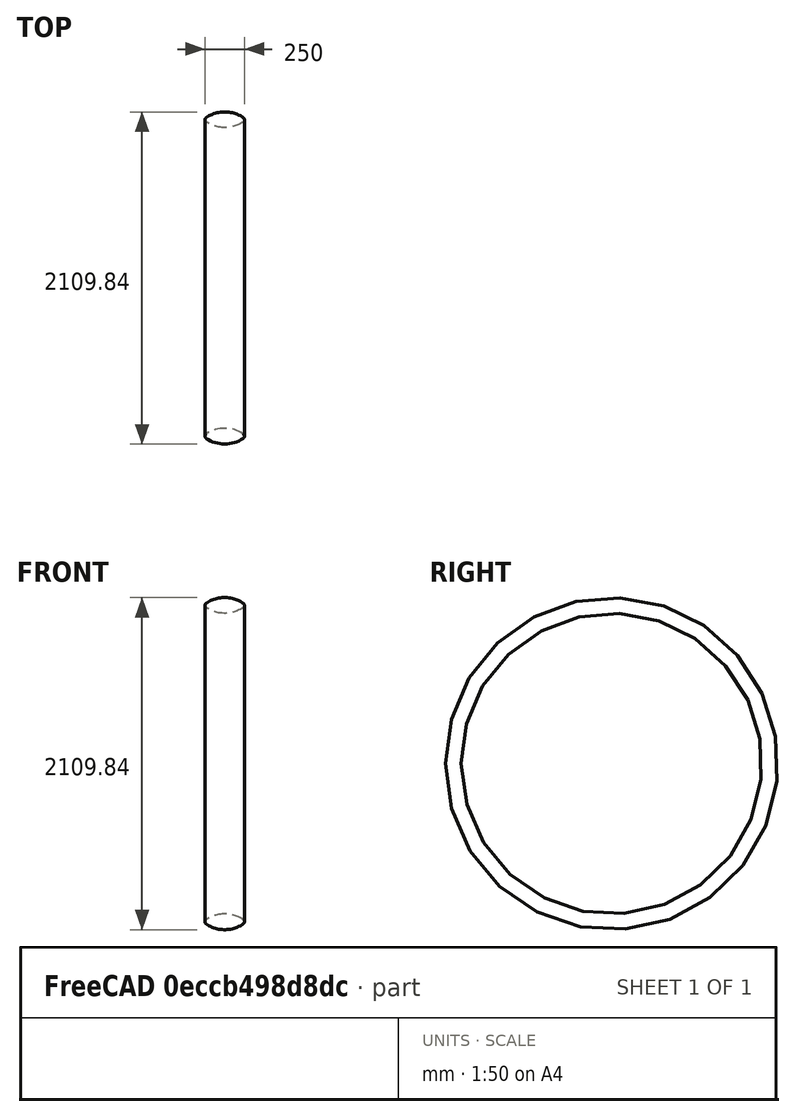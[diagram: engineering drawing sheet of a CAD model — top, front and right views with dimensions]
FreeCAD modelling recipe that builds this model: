
FCSTD DOCUMENT
Label: PR_003
objects: Sketcher::SketchObject×1, PartDesign::Revolution×1
note: 3 computed .brp shape members not serialized (recipe doc carries the construction recipe); baked Part::Feature solids carry a one-line shape summary decoded from their .brp

FEATURE [Sketcher::SketchObject] Sketch
  sketch-geometry (7):
    g0: LineSegment [constr] StartX=0 StartY=-954.92 StartZ=0 EndX=250 EndY=-954.92 EndZ=0
    g1: LineSegment [constr] StartX=0 StartY=-1054.92 StartZ=0 EndX=250 EndY=-1054.92 EndZ=0
    g2: ArcOfCircle CenterX=16.5179 CenterY=-1004.92 CenterZ=0 NormalX=0 NormalY=0 NormalZ=1 Radius=16.5179 StartAngle=2.16953 EndAngle=4.11366
    g3: ArcOfCircle CenterX=233.482 CenterY=-1004.92 CenterZ=0 NormalX=0 NormalY=0 NormalZ=1 Radius=16.5179 StartAngle=5.31112 EndAngle=7.25525
    g4: ArcOfCircle CenterX=125 CenterY=-845.92 CenterZ=0 NormalX=0 NormalY=0 NormalZ=1 Radius=209 StartAngle=4.11366 EndAngle=5.31112
    g5: ArcOfCircle CenterX=125 CenterY=-1163.92 CenterZ=0 NormalX=0 NormalY=0 NormalZ=1 Radius=209 StartAngle=0.972064 EndAngle=2.16953
    g6: LineSegment [constr] StartX=250 StartY=-1054.92 StartZ=0 EndX=250 EndY=-954.92 EndZ=0
  constraints (22):
    c: Horizontal(g0)
    c: DistanceY(g0) = -954.92
    c: Horizontal(g1)
    c: DistanceY(g0,g1) = -100
    c: Tangent(g1,g4)
    c: Radius(g4) = 209
    c: Radius(g5) = 209
    c: Tangent(g2,g5)
    c: Tangent(g5,g3)
    c: Tangent(g0,g5)
    c: DistanceX(g4) = 125
    c: DistanceX(g5) = 125
    c: DistanceX(g1) = 0
    c: DistanceX(g0) = 0
    c: DistanceX(g1) = 250
    c: Tangent(g3,g4)
    c: Tangent(g2,g4)
    c: Coincident(g6,g1)
    c: Vertical(g6)
    c: Tangent(g3,g6)
    c: Coincident(g6,g0)
    c: Tangent(g2,g-2)
FEATURE [PartDesign::Revolution] Revolution
  Angle = 360
  Axis = (1,0,0)
  Base = (0,0,0)
  ReferenceAxis = -> Sketch [H_Axis]
  Sketch = -> Sketch
